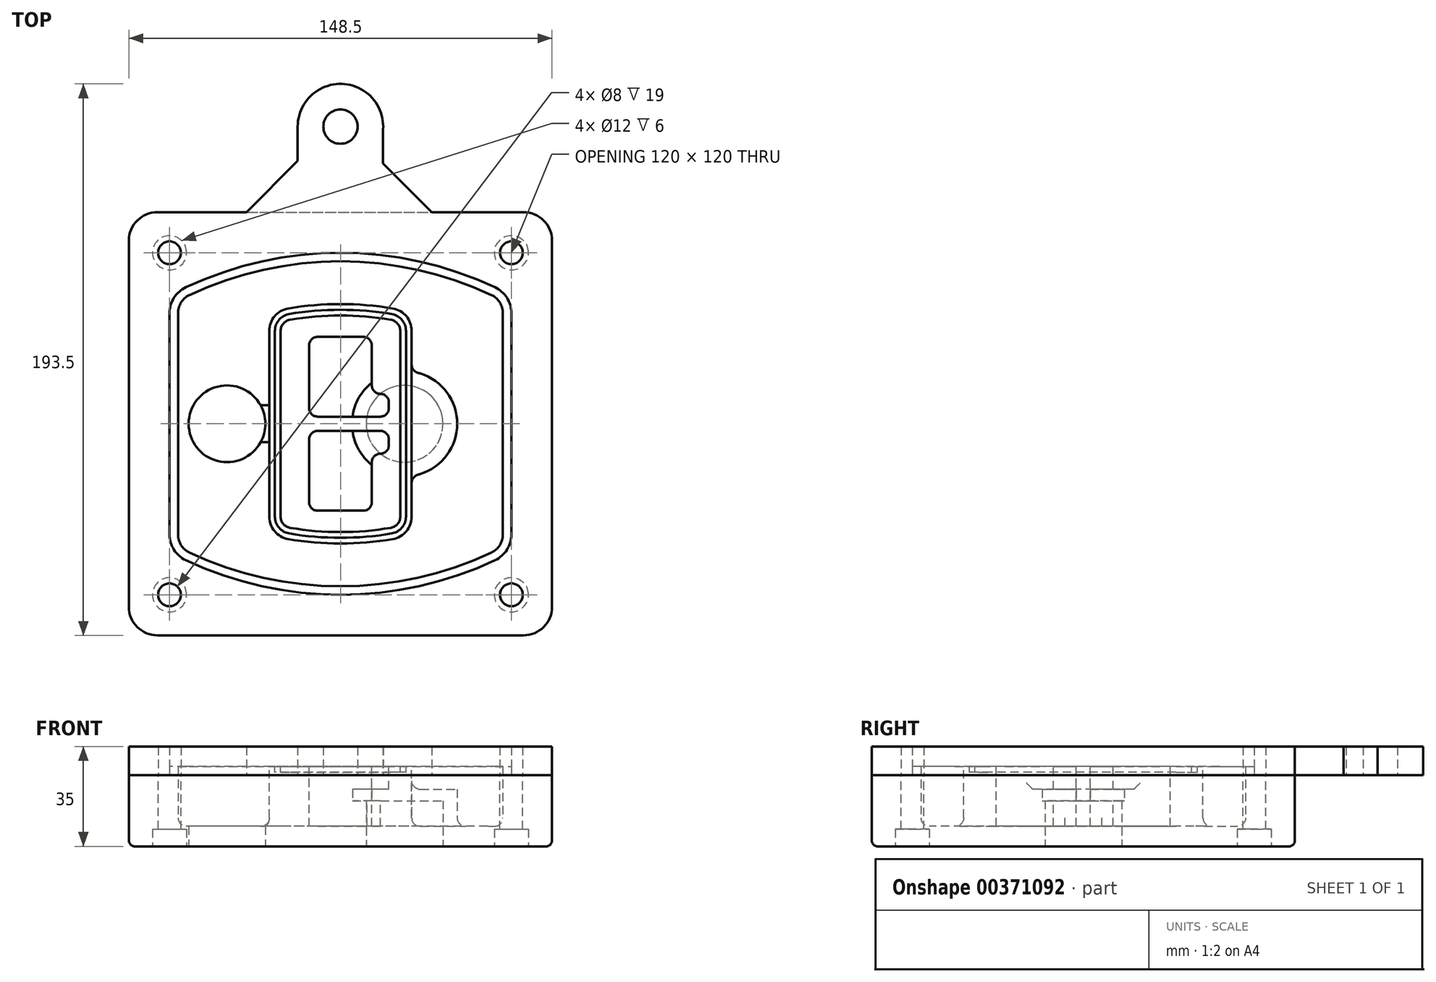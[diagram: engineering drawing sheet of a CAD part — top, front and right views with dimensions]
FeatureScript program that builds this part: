
annotation { "Feature Type Name" : "Feature", "Feature Type Description" : "" }
export const myFeature = defineFeature(function(context is Context, id is Id, definition is map)
    precondition{}
    {
        {
            var Q0;
            Q0=qCreatedBy(makeId("Top.planeOp"),FACE);
            var sketch = newSketch(context, id + "F0", { "sketchPlane" : qUnion([Q0])});
            skPoint(sketch, "E0.rect.middle", {"position": v(0, 0) * mm});
            skLineSegment(sketch, "E1.bottom", {"start": v(-64.25, -74.25) * mm, "end": v(64.25, -74.25) * mm});
            skLineSegment(sketch, "E1.top", {"start": v(-64.25, 74.25) * mm, "end": v(64.25, 74.25) * mm});
            skLineSegment(sketch, "E1.left", {"start": v(-74.25, -64.25) * mm, "end": v(-74.25, 64.25) * mm});
            skLineSegment(sketch, "E1.right", {"start": v(74.25, -64.25) * mm, "end": v(74.25, 64.25) * mm});
            skLineSegment(sketch, "E2", {"start": v(-74.25, 74.25) * mm, "end": v(74.25, -74.25) * mm, "construction": true});
            skLineSegment(sketch, "E3", {"start": v(74.25, 74.25) * mm, "end": v(-74.25, -74.25) * mm, "construction": true});
            skCircle(sketch, "E4", {"center": v(-60, 60) * mm, "radius": 4 * mm});
            skCircle(sketch, "E5", {"center": v(60, 60) * mm, "radius": 4 * mm});
            skCircle(sketch, "E6", {"center": v(60, -60) * mm, "radius": 4 * mm});
            skCircle(sketch, "E7", {"center": v(-60, -60) * mm, "radius": 4 * mm});
            skLineSegment(sketch, "E8", {"start": v(-60, 60) * mm, "end": v(60, 60) * mm, "construction": true});
            skLineSegment(sketch, "E9", {"start": v(60, 60) * mm, "end": v(60, -60) * mm, "construction": true});
            skLineSegment(sketch, "E10", {"start": v(60, -60) * mm, "end": v(-60, -60) * mm, "construction": true});
            skLineSegment(sketch, "E11", {"start": v(-60, -60) * mm, "end": v(-60, 60) * mm, "construction": true});
            skLineSegment(sketch, "E12", {"start": v(-60, 38.83) * mm, "end": v(-60, -38.83) * mm});
            skLineSegment(sketch, "E13", {"start": v(60, 38.83) * mm, "end": v(60, -38.83) * mm});
            skArc(sketch, "E14", {"start": v(54.26, 47.88) * mm, "mid": v(0, 60) * mm, "end": v(-54.26, 47.88) * mm});
            skArc(sketch, "E15", {"start": v(-54.26, -47.88) * mm, "mid": v(0, -60) * mm, "end": v(54.26, -47.88) * mm});
            skLineSegment(sketch, "E16", {"start": v(-60, 0) * mm, "end": v(60, 0) * mm, "construction": true});
            skPoint(sketch, "E17.visualSharp", {"position": v(-60, -45) * mm});
            skArc(sketch, "E17.filletArc", {"start": v(-60, -38.83) * mm, "mid": v(-58.44, -44.2) * mm, "end": v(-54.26, -47.88) * mm});
            skPoint(sketch, "E18.visualSharp", {"position": v(-60, 45) * mm});
            skArc(sketch, "E18.filletArc", {"start": v(-54.26, 47.88) * mm, "mid": v(-58.44, 44.2) * mm, "end": v(-60, 38.83) * mm});
            skPoint(sketch, "E19.visualSharp", {"position": v(60, 45) * mm});
            skArc(sketch, "E19.filletArc", {"start": v(60, 38.83) * mm, "mid": v(58.44, 44.2) * mm, "end": v(54.26, 47.88) * mm});
            skPoint(sketch, "E20.visualSharp", {"position": v(60, -45) * mm});
            skArc(sketch, "E20.filletArc", {"start": v(54.26, -47.88) * mm, "mid": v(58.44, -44.2) * mm, "end": v(60, -38.83) * mm});
            skPoint(sketch, "E21.visualSharp", {"position": v(-74.25, 74.25) * mm});
            skArc(sketch, "E21.filletArc", {"start": v(-64.25, 74.25) * mm, "mid": v(-71.32, 71.32) * mm, "end": v(-74.25, 64.25) * mm});
            skPoint(sketch, "E22.visualSharp", {"position": v(74.25, 74.25) * mm});
            skArc(sketch, "E22.filletArc", {"start": v(74.25, 64.25) * mm, "mid": v(71.32, 71.32) * mm, "end": v(64.25, 74.25) * mm});
            skPoint(sketch, "E23.visualSharp", {"position": v(74.25, -74.25) * mm});
            skArc(sketch, "E23.filletArc", {"start": v(64.25, -74.25) * mm, "mid": v(71.32, -71.32) * mm, "end": v(74.25, -64.25) * mm});
            skPoint(sketch, "E24.visualSharp", {"position": v(-74.25, -74.25) * mm});
            skArc(sketch, "E24.filletArc", {"start": v(-74.25, -64.25) * mm, "mid": v(-71.32, -71.32) * mm, "end": v(-64.25, -74.25) * mm});
            skArc(sketch, "E25.0", {"start": v(57, 38.83) * mm, "mid": v(55.9, 42.58) * mm, "end": v(52.98, 45.17) * mm});
            skLineSegment(sketch, "E25.1", {"start": v(57, 38.83) * mm, "end": v(57, -38.83) * mm});
            skArc(sketch, "E25.2", {"start": v(52.98, -45.17) * mm, "mid": v(55.9, -42.58) * mm, "end": v(57, -38.83) * mm});
            skArc(sketch, "E25.3", {"start": v(-52.98, -45.17) * mm, "mid": v(0, -57) * mm, "end": v(52.98, -45.17) * mm});
            skArc(sketch, "E25.4", {"start": v(-57, -38.83) * mm, "mid": v(-55.9, -42.58) * mm, "end": v(-52.98, -45.17) * mm});
            skArc(sketch, "E25.5", {"start": v(52.98, 45.17) * mm, "mid": v(0, 57) * mm, "end": v(-52.98, 45.17) * mm});
            skLineSegment(sketch, "E25.6", {"start": v(-57, 38.83) * mm, "end": v(-57, -38.83) * mm});
            skArc(sketch, "E25.7", {"start": v(-52.98, 45.17) * mm, "mid": v(-55.9, 42.58) * mm, "end": v(-57, 38.83) * mm});
            skArc(sketch, "E26.0", {"start": v(-55.96, 51.5) * mm, "mid": v(-61.82, 46.33) * mm, "end": v(-64, 38.83) * mm});
            skArc(sketch, "E26.1", {"start": v(55.96, 51.5) * mm, "mid": v(0, 64) * mm, "end": v(-55.96, 51.5) * mm});
            skArc(sketch, "E26.2", {"start": v(64, 38.83) * mm, "mid": v(61.82, 46.33) * mm, "end": v(55.96, 51.5) * mm});
            skLineSegment(sketch, "E26.3", {"start": v(64, 38.83) * mm, "end": v(64, -38.83) * mm});
            skArc(sketch, "E26.4", {"start": v(55.96, -51.5) * mm, "mid": v(61.82, -46.33) * mm, "end": v(64, -38.83) * mm});
            skLineSegment(sketch, "E26.5", {"start": v(-64, 38.83) * mm, "end": v(-64, -38.83) * mm});
            skArc(sketch, "E26.6", {"start": v(-55.96, -51.5) * mm, "mid": v(0, -64) * mm, "end": v(55.96, -51.5) * mm});
            skArc(sketch, "E26.7", {"start": v(-64, -38.83) * mm, "mid": v(-61.82, -46.33) * mm, "end": v(-55.96, -51.5) * mm});
            skSolve(sketch);
        }
        {
            var Q0;
            Q0=makeQuery(id+"F0.imprint","IMPRINT",FACE,{"disambiguationData":[TD([[makeQuery(id+"F0.imprint","IMPRINT",EDGE,{"derivedFrom":sQuery(id+"F0.wireOp",EDGE,"E1.bottom")}),1.0]])]});
            var Q1;
            Q1=makeQuery(id+"F0.imprint","IMPRINT",FACE,{"disambiguationData":[TD([[makeQuery(id+"F0.imprint","IMPRINT",EDGE,{"derivedFrom":sQuery(id+"F0.wireOp",EDGE,"E12")}),1.0]])]});
            var Q2;
            Q2=makeQuery(id+"F0.imprint","IMPRINT",FACE,{"disambiguationData":[TD([[makeQuery(id+"F0.imprint","IMPRINT",EDGE,{"derivedFrom":sQuery(id+"F0.wireOp",EDGE,"E25.0")}),1.0]])]});
            var Q3;
            Q3=makeQuery(id+"F0.imprint","IMPRINT",FACE,{"disambiguationData":[TD([[makeQuery(id+"F0.imprint","IMPRINT",EDGE,{"derivedFrom":sQuery(id+"F0.wireOp",EDGE,"E12")}),-1.0]])]});
            extrude(context, id + "F1", {"entities" : qUnion([Q0, Q1, Q2, Q3]), "oppositeDirection" : true, "depth" : 25 * mm});
        }
        {
            var Q0;
            Q0=makeQuery(id+"F0.imprint","IMPRINT",FACE,{"disambiguationData":[TD([[makeQuery(id+"F0.imprint","IMPRINT",EDGE,{"derivedFrom":sQuery(id+"F0.wireOp",EDGE,"E12")}),1.0]])]});
            extrude(context, id + "F2", {"entities" : qUnion([Q0]), "operationType" : NewBodyOperationType.ADD, "depth" : 3 * mm});
        }
        {
            var Q0;
            Q0=makeQuery(id+"F0.imprint","IMPRINT",FACE,{"disambiguationData":[TD([[makeQuery(id+"F0.imprint","IMPRINT",EDGE,{"derivedFrom":sQuery(id+"F0.wireOp",EDGE,"E25.0")}),1.0]])]});
            extrude(context, id + "F3", {"entities" : qUnion([Q0]), "operationType" : NewBodyOperationType.REMOVE, "oppositeDirection" : true, "depth" : 18 * mm});
        }
        {
            var Q0;
            Q0=makeQuery(id+"F2.opExtrude","CAP_FACE",FACE,{"disambiguationData":[OSD([sQuery(id+"F0.wireOp",EDGE,"E12"),sQuery(id+"F0.wireOp",EDGE,"E13"),sQuery(id+"F0.wireOp",EDGE,"E14"),sQuery(id+"F0.wireOp",EDGE,"E15"),sQuery(id+"F0.wireOp",EDGE,"E17.filletArc"),sQuery(id+"F0.wireOp",EDGE,"E18.filletArc"),sQuery(id+"F0.wireOp",EDGE,"E19.filletArc"),sQuery(id+"F0.wireOp",EDGE,"E20.filletArc"),sQuery(id+"F0.wireOp",EDGE,"E25.0"),sQuery(id+"F0.wireOp",EDGE,"E25.1"),sQuery(id+"F0.wireOp",EDGE,"E25.2"),sQuery(id+"F0.wireOp",EDGE,"E25.3"),sQuery(id+"F0.wireOp",EDGE,"E25.4"),sQuery(id+"F0.wireOp",EDGE,"E25.5"),sQuery(id+"F0.wireOp",EDGE,"E25.6"),sQuery(id+"F0.wireOp",EDGE,"E25.7")])],"isStart":false});
            var sketch = newSketch(context, id + "F4", { "sketchPlane" : qUnion([Q0])});
            skArc(sketch, "E27.0", {"start": v(-18.34, -40.45) * mm, "mid": v(0, -42) * mm, "end": v(18.34, -40.45) * mm});
            skArc(sketch, "E28.0", {"start": v(18.34, 40.45) * mm, "mid": v(0, 42) * mm, "end": v(-18.34, 40.45) * mm});
            skLineSegment(sketch, "E29", {"start": v(-25, 32.57) * mm, "end": v(-25, -32.57) * mm});
            skLineSegment(sketch, "E30", {"start": v(25, 32.57) * mm, "end": v(25, -32.57) * mm});
            skLineSegment(sketch, "E31", {"start": v(-25, 39.1) * mm, "end": v(25, 39.1) * mm, "construction": true});
            skLineSegment(sketch, "E32", {"start": v(-25, -39.1) * mm, "end": v(25, -39.1) * mm, "construction": true});
            skPoint(sketch, "E33.visualSharp", {"position": v(-25, 39.1) * mm});
            skArc(sketch, "E33.filletArc", {"start": v(-18.34, 40.45) * mm, "mid": v(-23.11, 37.73) * mm, "end": v(-25, 32.57) * mm});
            skPoint(sketch, "E34.visualSharp", {"position": v(25, 39.1) * mm});
            skArc(sketch, "E34.filletArc", {"start": v(25, 32.57) * mm, "mid": v(23.11, 37.73) * mm, "end": v(18.34, 40.45) * mm});
            skPoint(sketch, "E35.visualSharp", {"position": v(25, -39.1) * mm});
            skArc(sketch, "E35.filletArc", {"start": v(18.34, -40.45) * mm, "mid": v(23.11, -37.73) * mm, "end": v(25, -32.57) * mm});
            skPoint(sketch, "E36.visualSharp", {"position": v(-25, -39.1) * mm});
            skArc(sketch, "E36.filletArc", {"start": v(-25, -32.57) * mm, "mid": v(-23.11, -37.73) * mm, "end": v(-18.34, -40.45) * mm});
            skArc(sketch, "E37.0", {"start": v(52.98, 45.17) * mm, "mid": v(0, 57) * mm, "end": v(-52.98, 45.17) * mm});
            skArc(sketch, "E37.1", {"start": v(-52.98, 45.17) * mm, "mid": v(-55.9, 42.58) * mm, "end": v(-57, 38.83) * mm});
            skLineSegment(sketch, "E37.2", {"start": v(-57, 38.83) * mm, "end": v(-57, -38.83) * mm});
            skArc(sketch, "E37.3", {"start": v(-57, -38.83) * mm, "mid": v(-55.9, -42.58) * mm, "end": v(-52.98, -45.17) * mm});
            skArc(sketch, "E37.4", {"start": v(-52.98, -45.17) * mm, "mid": v(0, -57) * mm, "end": v(52.98, -45.17) * mm});
            skArc(sketch, "E37.5", {"start": v(52.98, -45.17) * mm, "mid": v(55.9, -42.58) * mm, "end": v(57, -38.83) * mm});
            skLineSegment(sketch, "E37.6", {"start": v(57, 38.83) * mm, "end": v(57, -38.83) * mm});
            skArc(sketch, "E37.7", {"start": v(57, 38.83) * mm, "mid": v(55.9, 42.58) * mm, "end": v(52.98, 45.17) * mm});
            skLineSegment(sketch, "E38.0", {"start": v(23, 32.57) * mm, "end": v(23, -32.57) * mm});
            skArc(sketch, "E38.1", {"start": v(18, -38.48) * mm, "mid": v(21.58, -36.44) * mm, "end": v(23, -32.57) * mm});
            skArc(sketch, "E38.2", {"start": v(-18, -38.48) * mm, "mid": v(0, -40) * mm, "end": v(18, -38.48) * mm});
            skArc(sketch, "E38.3", {"start": v(-23, -32.57) * mm, "mid": v(-21.58, -36.44) * mm, "end": v(-18, -38.48) * mm});
            skLineSegment(sketch, "E38.4", {"start": v(-23, 32.57) * mm, "end": v(-23, -32.57) * mm});
            skArc(sketch, "E38.5", {"start": v(23, 32.57) * mm, "mid": v(21.58, 36.44) * mm, "end": v(18, 38.48) * mm});
            skArc(sketch, "E38.6", {"start": v(-18, 38.48) * mm, "mid": v(-21.58, 36.44) * mm, "end": v(-23, 32.57) * mm});
            skArc(sketch, "E38.7", {"start": v(18, 38.48) * mm, "mid": v(0, 40) * mm, "end": v(-18, 38.48) * mm});
            skArc(sketch, "E39.0", {"start": v(21, 32.57) * mm, "mid": v(20.06, 35.15) * mm, "end": v(17.67, 36.5) * mm});
            skLineSegment(sketch, "E39.1", {"start": v(21, 32.57) * mm, "end": v(21, -32.57) * mm});
            skArc(sketch, "E39.2", {"start": v(17.67, -36.5) * mm, "mid": v(20.06, -35.15) * mm, "end": v(21, -32.57) * mm});
            skArc(sketch, "E39.3", {"start": v(-17.67, -36.5) * mm, "mid": v(0, -38) * mm, "end": v(17.67, -36.5) * mm});
            skArc(sketch, "E39.4", {"start": v(-21, -32.57) * mm, "mid": v(-20.06, -35.15) * mm, "end": v(-17.67, -36.5) * mm});
            skArc(sketch, "E39.5", {"start": v(17.67, 36.5) * mm, "mid": v(0, 38) * mm, "end": v(-17.67, 36.5) * mm});
            skLineSegment(sketch, "E39.6", {"start": v(-21, 32.57) * mm, "end": v(-21, -32.57) * mm});
            skArc(sketch, "E39.7", {"start": v(-17.67, 36.5) * mm, "mid": v(-20.06, 35.15) * mm, "end": v(-21, 32.57) * mm});
            skLineSegment(sketch, "E40", {"start": v(-25, 0) * mm, "end": v(25, 0) * mm, "construction": true});
            skLineSegment(sketch, "E41", {"start": v(-11, 5.5) * mm, "end": v(-11, 27.5) * mm});
            skLineSegment(sketch, "E42", {"start": v(-8, 30.5) * mm, "end": v(8, 30.5) * mm});
            skLineSegment(sketch, "E43", {"start": v(11, 27.5) * mm, "end": v(11, 13.5) * mm});
            skLineSegment(sketch, "E44", {"start": v(14, 10.5) * mm, "end": v(14, 10.5) * mm});
            skLineSegment(sketch, "E45", {"start": v(17, 7.5) * mm, "end": v(17, 5.5) * mm});
            skLineSegment(sketch, "E46", {"start": v(14, 2.5) * mm, "end": v(-8, 2.5) * mm});
            skPoint(sketch, "E47.visualSharp", {"position": v(-11, 30.5) * mm});
            skArc(sketch, "E47.filletArc", {"start": v(-8, 30.5) * mm, "mid": v(-10.12, 29.62) * mm, "end": v(-11, 27.5) * mm});
            skPoint(sketch, "E48.visualSharp", {"position": v(11, 30.5) * mm});
            skArc(sketch, "E48.filletArc", {"start": v(11, 27.5) * mm, "mid": v(10.12, 29.62) * mm, "end": v(8, 30.5) * mm});
            skPoint(sketch, "E49.visualSharp", {"position": v(11, 10.5) * mm});
            skArc(sketch, "E49.filletArc", {"start": v(11, 13.5) * mm, "mid": v(11.88, 11.38) * mm, "end": v(14, 10.5) * mm});
            skPoint(sketch, "E50.visualSharp", {"position": v(17, 10.5) * mm});
            skArc(sketch, "E50.filletArc", {"start": v(17, 7.5) * mm, "mid": v(16.12, 9.62) * mm, "end": v(14, 10.5) * mm});
            skPoint(sketch, "E51.visualSharp", {"position": v(17, 2.5) * mm});
            skArc(sketch, "E51.filletArc", {"start": v(14, 2.5) * mm, "mid": v(16.12, 3.38) * mm, "end": v(17, 5.5) * mm});
            skPoint(sketch, "E52.visualSharp", {"position": v(-11, 2.5) * mm});
            skArc(sketch, "E52.filletArc", {"start": v(-11, 5.5) * mm, "mid": v(-10.12, 3.38) * mm, "end": v(-8, 2.5) * mm});
            skLineSegment(sketch, "E53.0.MirrorCS", {"start": v(14, -2.5) * mm, "end": v(-8, -2.5) * mm});
            skArc(sketch, "E54.0.MirrorCS", {"start": v(-11, -5.5) * mm, "mid": v(-10.12, -3.38) * mm, "end": v(-8, -2.5) * mm});
            skLineSegment(sketch, "E55.0.MirrorCS", {"start": v(-11, -5.5) * mm, "end": v(-11, -27.5) * mm});
            skArc(sketch, "E56.0.MirrorCS", {"start": v(-8, -30.5) * mm, "mid": v(-10.12, -29.62) * mm, "end": v(-11, -27.5) * mm});
            skLineSegment(sketch, "E57.0.MirrorCS", {"start": v(-8, -30.5) * mm, "end": v(8, -30.5) * mm});
            skArc(sketch, "E58.0.MirrorCS", {"start": v(11, -27.5) * mm, "mid": v(10.12, -29.62) * mm, "end": v(8, -30.5) * mm});
            skLineSegment(sketch, "E59.0.MirrorCS", {"start": v(11, -27.5) * mm, "end": v(11, -13.5) * mm});
            skArc(sketch, "E60.0.MirrorCS", {"start": v(11, -13.5) * mm, "mid": v(11.88, -11.38) * mm, "end": v(14, -10.5) * mm});
            skArc(sketch, "E61.0.MirrorCS", {"start": v(17, -7.5) * mm, "mid": v(16.12, -9.62) * mm, "end": v(14, -10.5) * mm});
            skLineSegment(sketch, "E62.0.MirrorCS", {"start": v(17, -7.5) * mm, "end": v(17, -5.5) * mm});
            skArc(sketch, "E63.0.MirrorCS", {"start": v(14, -2.5) * mm, "mid": v(16.12, -3.38) * mm, "end": v(17, -5.5) * mm});
            skSolve(sketch);
        }
        {
            var Q0;
            Q0=makeQuery(id+"F4.imprint","IMPRINT",FACE,{"disambiguationData":[TD([[makeQuery(id+"F4.imprint","IMPRINT",EDGE,{"derivedFrom":sQuery(id+"F4.wireOp",EDGE,"E27.0")}),1.0]])]});
            var Q1;
            Q1=makeQuery(id+"F4.imprint","IMPRINT",FACE,{"disambiguationData":[TD([[makeQuery(id+"F4.imprint","IMPRINT",EDGE,{"derivedFrom":sQuery(id+"F4.wireOp",EDGE,"E38.0")}),-1.0]])]});
            var Q2;
            Q2=makeQuery(id+"F4.imprint","IMPRINT",FACE,{"disambiguationData":[TD([[makeQuery(id+"F4.imprint","IMPRINT",EDGE,{"derivedFrom":sQuery(id+"F4.wireOp",EDGE,"E39.0")}),1.0]])]});
            extrude(context, id + "F5", {"entities" : qUnion([Q0, Q1, Q2]), "operationType" : NewBodyOperationType.ADD, "endBound" : BoundingType.UP_TO_NEXT, "oppositeDirection" : true, "depth" : 25 * mm});
        }
        {
            var Q0;
            Q0=makeQuery(id+"F4.imprint","IMPRINT",FACE,{"disambiguationData":[TD([[makeQuery(id+"F4.imprint","IMPRINT",EDGE,{"derivedFrom":sQuery(id+"F4.wireOp",EDGE,"E38.0")}),-1.0]])]});
            extrude(context, id + "F6", {"entities" : qUnion([Q0]), "operationType" : NewBodyOperationType.REMOVE, "oppositeDirection" : true, "depth" : 2 * mm});
        }
        {
            var Q0;
            Q0=makeQuery(id+"F1.opExtrude","CAP_FACE",FACE,{"disambiguationData":[OSD([sQuery(id+"F0.wireOp",EDGE,"E1.bottom"),sQuery(id+"F0.wireOp",EDGE,"E1.top"),sQuery(id+"F0.wireOp",EDGE,"E1.left"),sQuery(id+"F0.wireOp",EDGE,"E1.right"),sQuery(id+"F0.wireOp",EDGE,"E4"),sQuery(id+"F0.wireOp",EDGE,"E5"),sQuery(id+"F0.wireOp",EDGE,"E6"),sQuery(id+"F0.wireOp",EDGE,"E7"),sQuery(id+"F0.wireOp",EDGE,"E21.filletArc"),sQuery(id+"F0.wireOp",EDGE,"E22.filletArc"),sQuery(id+"F0.wireOp",EDGE,"E23.filletArc"),sQuery(id+"F0.wireOp",EDGE,"E24.filletArc")])],"isStart":false});
            var sketch = newSketch(context, id + "F7", { "sketchPlane" : qUnion([Q0])});
            skCircle(sketch, "E64", {"center": v(22.5, 0) * mm, "radius": 13.47 * mm});
            skCircle(sketch, "E65", {"center": v(-39.81, 0) * mm, "radius": 13.47 * mm});
            skLineSegment(sketch, "E66", {"start": v(74.25, 0) * mm, "end": v(-74.25, 0) * mm});
            skCircle(sketch, "E67", {"center": v(22.5, 0) * mm, "radius": 18.47 * mm});
            skCircle(sketch, "E68", {"center": v(60, -60) * mm, "radius": 6 * mm});
            skCircle(sketch, "E69", {"center": v(-60, -60) * mm, "radius": 6 * mm});
            skCircle(sketch, "E70", {"center": v(-60, 60) * mm, "radius": 6 * mm});
            skCircle(sketch, "E71", {"center": v(60, 60) * mm, "radius": 6 * mm});
            skSolve(sketch);
        }
        {
            var Q0;
            {var subQ1=sQuery(id+"F7.wireOp",EDGE,"E66");var subQ4=sQuery(id+"F7.wireOp",EDGE,"E64");var subQ6=makeQuery(id+"F7.imprint","INTERSECT",VERTEX,{"disambiguationData":[OD(0.0)],"derivedFrom":[subQ4,subQ1]});Q0=makeQuery(id+"F7.imprint","IMPRINT",FACE,{"disambiguationData":[TD([[makeQuery(id+"F7.imprint","IMPRINT",EDGE,{"disambiguationData":[TD([[subQ6,-1.0]])],"derivedFrom":subQ4}),-1.0]])]});}
            var Q1;
            {var subQ0=sQuery(id+"F7.wireOp",EDGE,"E66");var subQ1=sQuery(id+"F7.wireOp",EDGE,"E64");var subQ3=makeQuery(id+"F7.imprint","INTERSECT",VERTEX,{"disambiguationData":[OD(0.0)],"derivedFrom":[subQ1,subQ0]});Q1=makeQuery(id+"F7.imprint","IMPRINT",FACE,{"disambiguationData":[TD([[makeQuery(id+"F7.imprint","IMPRINT",EDGE,{"disambiguationData":[TD([[subQ3,-1.0]])],"derivedFrom":subQ1}),1.0]])]});}
            var Q2;
            {var subQ0=sQuery(id+"F7.wireOp",EDGE,"E66");var subQ1=sQuery(id+"F7.wireOp",EDGE,"E64");var subQ3=makeQuery(id+"F7.imprint","INTERSECT",VERTEX,{"disambiguationData":[OD(0.0)],"derivedFrom":[subQ1,subQ0]});Q2=makeQuery(id+"F7.imprint","IMPRINT",FACE,{"disambiguationData":[TD([[makeQuery(id+"F7.imprint","IMPRINT",EDGE,{"disambiguationData":[TD([[subQ3,1.0]])],"derivedFrom":subQ1}),1.0]])]});}
            var Q3;
            {var subQ1=sQuery(id+"F7.wireOp",EDGE,"E66");var subQ4=sQuery(id+"F7.wireOp",EDGE,"E64");var subQ6=makeQuery(id+"F7.imprint","INTERSECT",VERTEX,{"disambiguationData":[OD(0.0)],"derivedFrom":[subQ4,subQ1]});Q3=makeQuery(id+"F7.imprint","IMPRINT",FACE,{"disambiguationData":[TD([[makeQuery(id+"F7.imprint","IMPRINT",EDGE,{"disambiguationData":[TD([[subQ6,1.0]])],"derivedFrom":subQ4}),-1.0]])]});}
            extrude(context, id + "F8", {"entities" : qUnion([Q0, Q1, Q2, Q3]), "operationType" : NewBodyOperationType.ADD, "oppositeDirection" : true, "depth" : 20 * mm});
        }
        {
            var Q0;
            {var subQ0=sQuery(id+"F7.wireOp",EDGE,"E66");var subQ1=sQuery(id+"F7.wireOp",EDGE,"E64");var subQ3=makeQuery(id+"F7.imprint","INTERSECT",VERTEX,{"disambiguationData":[OD(0.0)],"derivedFrom":[subQ1,subQ0]});Q0=makeQuery(id+"F7.imprint","IMPRINT",FACE,{"disambiguationData":[TD([[makeQuery(id+"F7.imprint","IMPRINT",EDGE,{"disambiguationData":[TD([[subQ3,-1.0]])],"derivedFrom":subQ1}),1.0]])]});}
            var Q1;
            {var subQ0=sQuery(id+"F7.wireOp",EDGE,"E66");var subQ1=sQuery(id+"F7.wireOp",EDGE,"E64");var subQ3=makeQuery(id+"F7.imprint","INTERSECT",VERTEX,{"disambiguationData":[OD(0.0)],"derivedFrom":[subQ1,subQ0]});Q1=makeQuery(id+"F7.imprint","IMPRINT",FACE,{"disambiguationData":[TD([[makeQuery(id+"F7.imprint","IMPRINT",EDGE,{"disambiguationData":[TD([[subQ3,1.0]])],"derivedFrom":subQ1}),1.0]])]});}
            extrude(context, id + "F9", {"entities" : qUnion([Q0, Q1]), "operationType" : NewBodyOperationType.REMOVE, "oppositeDirection" : true, "depth" : 16 * mm});
        }
        {
            var Q0;
            {var subQ0=sQuery(id+"F7.wireOp",EDGE,"E66");var subQ1=sQuery(id+"F7.wireOp",EDGE,"E65");var subQ3=makeQuery(id+"F7.imprint","INTERSECT",VERTEX,{"disambiguationData":[OD(0.0)],"derivedFrom":[subQ1,subQ0]});Q0=makeQuery(id+"F7.imprint","IMPRINT",FACE,{"disambiguationData":[TD([[makeQuery(id+"F7.imprint","IMPRINT",EDGE,{"disambiguationData":[TD([[subQ3,-1.0]])],"derivedFrom":subQ1}),1.0]])]});}
            var Q1;
            {var subQ0=sQuery(id+"F7.wireOp",EDGE,"E66");var subQ1=sQuery(id+"F7.wireOp",EDGE,"E65");var subQ3=makeQuery(id+"F7.imprint","INTERSECT",VERTEX,{"disambiguationData":[OD(0.0)],"derivedFrom":[subQ1,subQ0]});Q1=makeQuery(id+"F7.imprint","IMPRINT",FACE,{"disambiguationData":[TD([[makeQuery(id+"F7.imprint","IMPRINT",EDGE,{"disambiguationData":[TD([[subQ3,1.0]])],"derivedFrom":subQ1}),1.0]])]});}
            extrude(context, id + "F10", {"entities" : qUnion([Q0, Q1]), "operationType" : NewBodyOperationType.REMOVE, "oppositeDirection" : true, "depth" : 25 * mm});
        }
        {
            var Q0;
            Q0=makeQuery(id+"F7.imprint","IMPRINT",FACE,{"disambiguationData":[TD([[makeQuery(id+"F7.imprint","IMPRINT",EDGE,{"derivedFrom":sQuery(id+"F7.wireOp",EDGE,"E68")}),1.0]])]});
            var Q1;
            Q1=makeQuery(id+"F7.imprint","IMPRINT",FACE,{"disambiguationData":[TD([[makeQuery(id+"F7.imprint","IMPRINT",EDGE,{"derivedFrom":makeQuery(id+"F1.opExtrude","CAP_EDGE",EDGE,{"disambiguationData":[OSD([sQuery(id+"F0.wireOp",EDGE,"E5")])],"isStart":false})}),-1.0]])]});
            var Q2;
            Q2=makeQuery(id+"F7.imprint","IMPRINT",FACE,{"disambiguationData":[TD([[makeQuery(id+"F7.imprint","IMPRINT",EDGE,{"derivedFrom":sQuery(id+"F7.wireOp",EDGE,"E69")}),1.0]])]});
            var Q3;
            Q3=makeQuery(id+"F7.imprint","IMPRINT",FACE,{"disambiguationData":[TD([[makeQuery(id+"F7.imprint","IMPRINT",EDGE,{"derivedFrom":makeQuery(id+"F1.opExtrude","CAP_EDGE",EDGE,{"disambiguationData":[OSD([sQuery(id+"F0.wireOp",EDGE,"E4")])],"isStart":false})}),-1.0]])]});
            var Q4;
            Q4=makeQuery(id+"F7.imprint","IMPRINT",FACE,{"disambiguationData":[TD([[makeQuery(id+"F7.imprint","IMPRINT",EDGE,{"derivedFrom":sQuery(id+"F7.wireOp",EDGE,"E70")}),1.0]])]});
            var Q5;
            Q5=makeQuery(id+"F7.imprint","IMPRINT",FACE,{"disambiguationData":[TD([[makeQuery(id+"F7.imprint","IMPRINT",EDGE,{"derivedFrom":makeQuery(id+"F1.opExtrude","CAP_EDGE",EDGE,{"disambiguationData":[OSD([sQuery(id+"F0.wireOp",EDGE,"E7")])],"isStart":false})}),-1.0]])]});
            var Q6;
            Q6=makeQuery(id+"F7.imprint","IMPRINT",FACE,{"disambiguationData":[TD([[makeQuery(id+"F7.imprint","IMPRINT",EDGE,{"derivedFrom":sQuery(id+"F7.wireOp",EDGE,"E71")}),1.0]])]});
            var Q7;
            Q7=makeQuery(id+"F7.imprint","IMPRINT",FACE,{"disambiguationData":[TD([[makeQuery(id+"F7.imprint","IMPRINT",EDGE,{"derivedFrom":makeQuery(id+"F1.opExtrude","CAP_EDGE",EDGE,{"disambiguationData":[OSD([sQuery(id+"F0.wireOp",EDGE,"E6")])],"isStart":false})}),-1.0]])]});
            extrude(context, id + "F11", {"entities" : qUnion([Q0, Q1, Q2, Q3, Q4, Q5, Q6, Q7]), "operationType" : NewBodyOperationType.REMOVE, "oppositeDirection" : true, "depth" : 6 * mm});
        }
        {
            var Q0;
            Q0=makeQuery(id+"F9.boolean.opBoolean","COPY",FACE,{"derivedFrom":makeQuery(id+"F9.opExtrude","CAP_FACE",FACE,{"disambiguationData":[OSD([sQuery(id+"F7.wireOp",EDGE,"E64")])],"isStart":false})});
            var sketch = newSketch(context, id + "F12", { "sketchPlane" : qUnion([Q0])});
            skArc(sketch, "E72.0", {"start": v(11, 14.45) * mm, "mid": v(6.45, 9.13) * mm, "end": v(4.2, 2.5) * mm});
            skArc(sketch, "E72.1", {"start": v(4.2, -2.5) * mm, "mid": v(6.45, -9.13) * mm, "end": v(11, -14.45) * mm});
            skLineSegment(sketch, "E73", {"start": v(4.2, -2.5) * mm, "end": v(14, -2.5) * mm});
            skLineSegment(sketch, "E74.0", {"start": v(14, 2.5) * mm, "end": v(4.2, 2.5) * mm});
            skArc(sketch, "E74.1", {"start": v(14, 2.5) * mm, "mid": v(16.12, 3.38) * mm, "end": v(17, 5.5) * mm});
            skLineSegment(sketch, "E74.2", {"start": v(17, 7.5) * mm, "end": v(17, 5.5) * mm});
            skArc(sketch, "E74.3", {"start": v(17, 7.5) * mm, "mid": v(16.12, 9.62) * mm, "end": v(14, 10.5) * mm});
            skArc(sketch, "E74.4", {"start": v(11, 13.5) * mm, "mid": v(11.88, 11.38) * mm, "end": v(14, 10.5) * mm});
            skLineSegment(sketch, "E74.5", {"start": v(11, 14.45) * mm, "end": v(11, 13.5) * mm});
            skLineSegment(sketch, "E74.7", {"start": v(14, -2.5) * mm, "end": v(4.2, -2.5) * mm});
            skArc(sketch, "E74.8", {"start": v(14, -2.5) * mm, "mid": v(16.12, -3.38) * mm, "end": v(17, -5.5) * mm});
            skLineSegment(sketch, "E74.9", {"start": v(17, -7.5) * mm, "end": v(17, -5.5) * mm});
            skArc(sketch, "E74.10", {"start": v(17, -7.5) * mm, "mid": v(16.12, -9.62) * mm, "end": v(14, -10.5) * mm});
            skArc(sketch, "E74.11", {"start": v(11, -13.5) * mm, "mid": v(11.88, -11.38) * mm, "end": v(14, -10.5) * mm});
            skLineSegment(sketch, "E74.12", {"start": v(11, -14.45) * mm, "end": v(11, -13.5) * mm});
            skPoint(sketch, "E75.orphan", {"position": v(11, -27.5) * mm});
            skPoint(sketch, "E76.orphan", {"position": v(-8, -2.5) * mm});
            skPoint(sketch, "E77.orphan", {"position": v(-8, 2.5) * mm});
            skPoint(sketch, "E78.orphan", {"position": v(11, 27.5) * mm});
            skSolve(sketch);
        }
        {
            var Q0;
            {var subQ7=sQuery(id+"F12.wireOp",EDGE,"E72.0");var subQ14=sQuery(id+"F12.wireOp",EDGE,"E72.1");var subQ16=sQuery(id+"F12.wireOp",EDGE,"E74.1");var subQ18=sQuery(id+"F12.wireOp",EDGE,"E74.8");Q0=qUnion([makeQuery(id+"F12.imprint","IMPRINT",FACE,{"disambiguationData":[TD([[makeQuery(id+"F12.imprint","IMPRINT",EDGE,{"derivedFrom":subQ7}),1.0]])]}),makeQuery(id+"F12.imprint","IMPRINT",FACE,{"disambiguationData":[TD([[makeQuery(id+"F12.imprint","IMPRINT",EDGE,{"derivedFrom":subQ14}),1.0]])]}),makeQuery(id+"F12.imprint","IMPRINT",FACE,{"disambiguationData":[TD([[makeQuery(id+"F12.imprint","IMPRINT",EDGE,{"derivedFrom":subQ16}),1.0]])]}),makeQuery(id+"F12.imprint","IMPRINT",FACE,{"disambiguationData":[TD([[makeQuery(id+"F12.imprint","IMPRINT",EDGE,{"derivedFrom":subQ18}),-1.0]])]})]);}
            var Q1;
            Q1=makeQuery(id+"F5.boolean.opBoolean","SPLIT",FACE,{"disambiguationData":[TD([makeQuery(id+"F5.opExtrude","SWEPT_FACE",FACE,{"disambiguationData":[OSD([sQuery(id+"F4.wireOp",EDGE,"E41")])]})])],"derivedFrom":makeQuery(id+"F3.boolean.opBoolean","COPY",FACE,{"derivedFrom":makeQuery(id+"F3.opExtrude","CAP_FACE",FACE,{"disambiguationData":[OSD([sQuery(id+"F0.wireOp",EDGE,"E25.0"),sQuery(id+"F0.wireOp",EDGE,"E25.1"),sQuery(id+"F0.wireOp",EDGE,"E25.2"),sQuery(id+"F0.wireOp",EDGE,"E25.3"),sQuery(id+"F0.wireOp",EDGE,"E25.4"),sQuery(id+"F0.wireOp",EDGE,"E25.5"),sQuery(id+"F0.wireOp",EDGE,"E25.6"),sQuery(id+"F0.wireOp",EDGE,"E25.7")])],"isStart":false})})});
            extrude(context, id + "F13", {"entities" : qUnion([Q0]), "operationType" : NewBodyOperationType.REMOVE, "endBound" : BoundingType.UP_TO_SURFACE, "endBoundEntityFace" : qUnion([Q1]), "depth" : 25 * mm});
        }
        {
            var Q0;
            Q0=makeQuery(id+"F3.boolean.opBoolean","COPY",EDGE,{"derivedFrom":makeQuery(id+"F3.opExtrude","CAP_EDGE",EDGE,{"disambiguationData":[OSD([sQuery(id+"F0.wireOp",EDGE,"E25.6")])],"isStart":false})});
            var Q1;
            Q1=makeQuery(id+"F8.boolean.opBoolean","INTERSECT",EDGE,{"derivedFrom":[makeQuery(id+"F5.opExtrude","SWEPT_FACE",FACE,{"disambiguationData":[OSD([sQuery(id+"F4.wireOp",EDGE,"E30")])]}),makeQuery(id+"F8.opExtrude","CAP_FACE",FACE,{"disambiguationData":[OSD([sQuery(id+"F7.wireOp",EDGE,"E67")])],"isStart":false})]});
            var Q2;
            Q2=makeQuery(id+"F8.boolean.opBoolean","INTERSECT",EDGE,{"disambiguationData":[OD(1.0)],"derivedFrom":[makeQuery(id+"F5.opExtrude","SWEPT_FACE",FACE,{"disambiguationData":[OSD([sQuery(id+"F4.wireOp",EDGE,"E30")])]}),makeQuery(id+"F8.opExtrude","SWEPT_FACE",FACE,{"disambiguationData":[OSD([sQuery(id+"F7.wireOp",EDGE,"E67")])]})]});
            var Q3;
            {var subQ0=sQuery(id+"F4.wireOp",EDGE,"E30");Q3=makeQuery(id+"F8.boolean.opBoolean","SPLIT",EDGE,{"disambiguationData":[TD([makeQuery(id+"F5.opExtrude","SWEPT_FACE",FACE,{"disambiguationData":[OSD([sQuery(id+"F4.wireOp",EDGE,"E35.filletArc")])]})])],"derivedFrom":makeQuery(id+"F5.opExtrude","CAP_EDGE",EDGE,{"disambiguationData":[OSD([subQ0])],"isStart":false})});}
            var Q4;
            {var subQ0=sQuery(id+"F0.wireOp",EDGE,"E25.7");var subQ1=sQuery(id+"F0.wireOp",EDGE,"E25.1");var subQ2=sQuery(id+"F0.wireOp",EDGE,"E25.6");var subQ3=sQuery(id+"F0.wireOp",EDGE,"E25.5");var subQ4=sQuery(id+"F0.wireOp",EDGE,"E25.4");var subQ5=sQuery(id+"F0.wireOp",EDGE,"E25.0");var subQ6=sQuery(id+"F0.wireOp",EDGE,"E25.2");var subQ7=sQuery(id+"F0.wireOp",EDGE,"E25.3");Q4=makeQuery(id+"F8.boolean.opBoolean","INTERSECT",EDGE,{"derivedFrom":[makeQuery(id+"F5.boolean.opBoolean","SPLIT",FACE,{"disambiguationData":[TD([makeQuery(id+"F2.opExtrude","SWEPT_FACE",FACE,{"disambiguationData":[OSD([subQ5])]})])],"derivedFrom":makeQuery(id+"F3.boolean.opBoolean","COPY",FACE,{"derivedFrom":makeQuery(id+"F3.opExtrude","CAP_FACE",FACE,{"disambiguationData":[OSD([subQ5,subQ1,subQ6,subQ7,subQ4,subQ3,subQ2,subQ0])],"isStart":false})})}),makeQuery(id+"F8.opExtrude","SWEPT_FACE",FACE,{"disambiguationData":[OSD([sQuery(id+"F7.wireOp",EDGE,"E67")])]})]});}
            var Q5;
            Q5=makeQuery(id+"F8.boolean.opBoolean","INTERSECT",EDGE,{"disambiguationData":[OD(0.0)],"derivedFrom":[makeQuery(id+"F5.opExtrude","SWEPT_FACE",FACE,{"disambiguationData":[OSD([sQuery(id+"F4.wireOp",EDGE,"E30")])]}),makeQuery(id+"F8.opExtrude","SWEPT_FACE",FACE,{"disambiguationData":[OSD([sQuery(id+"F7.wireOp",EDGE,"E67")])]})]});
            fillet(context, id + "F14", {"entities" : qUnion([Q0, Q1, Q2, Q3, Q4, Q5]), "radius" : 3 * mm, "tangentPropagation" : true, "allowEdgeOverflow" : false});
        }
        {
            var Q0;
            Q0=makeQuery(id+"F1.opExtrude","CAP_EDGE",EDGE,{"disambiguationData":[OSD([sQuery(id+"F0.wireOp",EDGE,"E1.bottom")])],"isStart":false});
            fillet(context, id + "F15", {"entities" : qUnion([Q0]), "radius" : 2 * mm, "tangentPropagation" : true, "allowEdgeOverflow" : false});
        }
        {
            var Q0;
            {var subQ0=sQuery(id+"F0.wireOp",EDGE,"E21.filletArc");var subQ1=sQuery(id+"F0.wireOp",EDGE,"E7");var subQ2=sQuery(id+"F0.wireOp",EDGE,"E6");var subQ3=sQuery(id+"F0.wireOp",EDGE,"E5");var subQ4=sQuery(id+"F0.wireOp",EDGE,"E4");var subQ5=sQuery(id+"F0.wireOp",EDGE,"E22.filletArc");var subQ6=sQuery(id+"F0.wireOp",EDGE,"E1.bottom");var subQ7=sQuery(id+"F0.wireOp",EDGE,"E1.right");var subQ8=sQuery(id+"F0.wireOp",EDGE,"E1.top");var subQ9=sQuery(id+"F0.wireOp",EDGE,"E1.left");var subQ10=sQuery(id+"F0.wireOp",EDGE,"E23.filletArc");var subQ11=sQuery(id+"F0.wireOp",EDGE,"E24.filletArc");Q0=makeQuery(id+"F2.boolean.opBoolean","SPLIT",FACE,{"disambiguationData":[TD([makeQuery(id+"F1.opExtrude","SWEPT_FACE",FACE,{"disambiguationData":[OSD([subQ6])]})])],"derivedFrom":makeQuery(id+"F1.opExtrude","CAP_FACE",FACE,{"disambiguationData":[OSD([subQ6,subQ8,subQ9,subQ7,subQ4,subQ3,subQ2,subQ1,subQ0,subQ5,subQ10,subQ11])],"isStart":true})});}
            var sketch = newSketch(context, id + "F16", { "sketchPlane" : qUnion([Q0])});
            skCircle(sketch, "E79", {"center": v(0, 104.25) * mm, "radius": 6 * mm});
            skArc(sketch, "E80", {"start": v(14.97, 103.32) * mm, "mid": v(0.47, 119.24) * mm, "end": v(-15, 104.25) * mm});
            skLineSegment(sketch, "E81", {"start": v(-15, 104.25) * mm, "end": v(-15, 92.25) * mm});
            skLineSegment(sketch, "E82", {"start": v(-15, 92.25) * mm, "end": v(-33, 74.25) * mm});
            skLineSegment(sketch, "E83", {"start": v(14.97, 103.32) * mm, "end": v(14.97, 91.32) * mm});
            skLineSegment(sketch, "E84", {"start": v(14.97, 91.32) * mm, "end": v(32.04, 74.25) * mm});
            skArc(sketch, "E85.MirrorCS", {"start": v(14.97, -103.32) * mm, "mid": v(0.47, -119.24) * mm, "end": v(-15, -104.25) * mm});
            skCircle(sketch, "E86.MirrorC", {"center": v(0, -104.25) * mm, "radius": 6 * mm});
            skLineSegment(sketch, "E87.MirrorCS", {"start": v(-15, -104.25) * mm, "end": v(-15, -92.25) * mm});
            skLineSegment(sketch, "E88.MirrorCS", {"start": v(14.97, -103.32) * mm, "end": v(14.97, -91.32) * mm});
            skLineSegment(sketch, "E89.MirrorCS", {"start": v(14.97, -91.32) * mm, "end": v(32.04, -74.25) * mm});
            skLineSegment(sketch, "E90.MirrorCS", {"start": v(-15, -92.25) * mm, "end": v(-33, -74.25) * mm});
            skSolve(sketch);
        }
        {
            var Q0;
            Q0=makeQuery(id+"F16.imprint","IMPRINT",FACE,{"disambiguationData":[TD([[makeQuery(id+"F16.imprint","IMPRINT",EDGE,{"derivedFrom":sQuery(id+"F16.wireOp",EDGE,"fe3572da-cad3-4527-88be-e887dbe093910.MirrorC")}),-1.0]])]});
            var Q1;
            Q1=makeQuery(id+"F16.imprint","IMPRINT",FACE,{"disambiguationData":[TD([[makeQuery(id+"F16.imprint","IMPRINT",EDGE,{"derivedFrom":sQuery(id+"F16.wireOp",EDGE,"E85.MirrorCS")}),-1.0]])]});
            var Q2;
            Q2=makeQuery(id+"F16.imprint","IMPRINT",FACE,{"disambiguationData":[TD([[makeQuery(id+"F16.imprint","IMPRINT",EDGE,{"derivedFrom":sQuery(id+"F16.wireOp",EDGE,"E79")}),-1.0]])]});
            var Q3;
            Q3=makeQuery(id+"F16.imprint","IMPRINT",FACE,{"disambiguationData":[TD([[makeQuery(id+"F16.imprint","IMPRINT",EDGE,{"derivedFrom":makeQuery(id+"F1.opExtrude","CAP_EDGE",EDGE,{"disambiguationData":[OSD([sQuery(id+"F0.wireOp",EDGE,"E1.left")])],"isStart":true})}),-1.0]])]});
            extrude(context, id + "F17", {"entities" : qUnion([Q0, Q1, Q2, Q3]), "depth" : 10 * mm});
        }
    });
